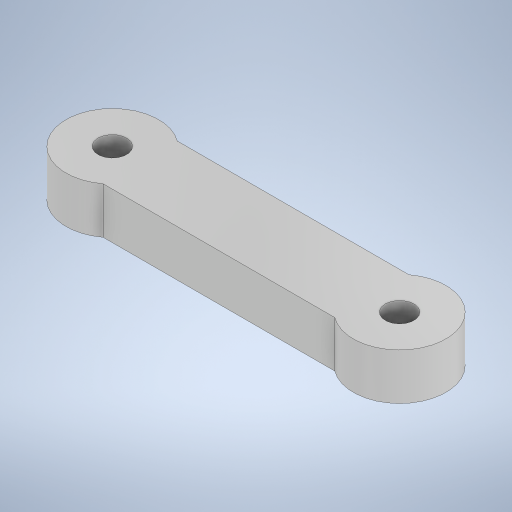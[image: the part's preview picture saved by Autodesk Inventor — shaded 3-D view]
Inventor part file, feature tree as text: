
AUTODESK INVENTOR PART (.ipt)
format: ipt  version: 2024.2 (Build 282272000, 272)  size: 241,664 bytes
history: native  units: in
note: dims shown in document units (in); Inventor stores cm internally (conversion verified against a paired STEP export)
features: sketch x2, extrude x1, hole x1, plane x1, projected_geometry x1
ambient origin geometry x8: Origin, YZ Plane, XZ Plane, XY Plane, X Axis, Y Axis, Z Axis, Center Point
bodies: Solid1 (feature_tree)
feature tree (6):
  extrude  "Extrusion1"  Depth=0.3937in
  hole  "Hole1"  [1 undecoded]
  plane  "Work Plane1"
  sketch  "Sketch1"  dims[d0=0.3937in d1=0.3937in]
  sketch  "Sketch2"  dims[d2=0.1575in d3=0.1575in d6=0.1969in d7=0.0in d8=0.122in d9=0.1575in d10=0.1575in d11=0.0787in d12=90.0deg d13=0.1575in d14=0.0in d18=-0.1378in d27=0.9843in]
  projected_geometry  "Projected Loop1"
note: 1 required parameter value undecoded (feature->parameter linkage not recoverable at this tier; creation-order binding heuristic only, values carry confidence <= 0.55)
